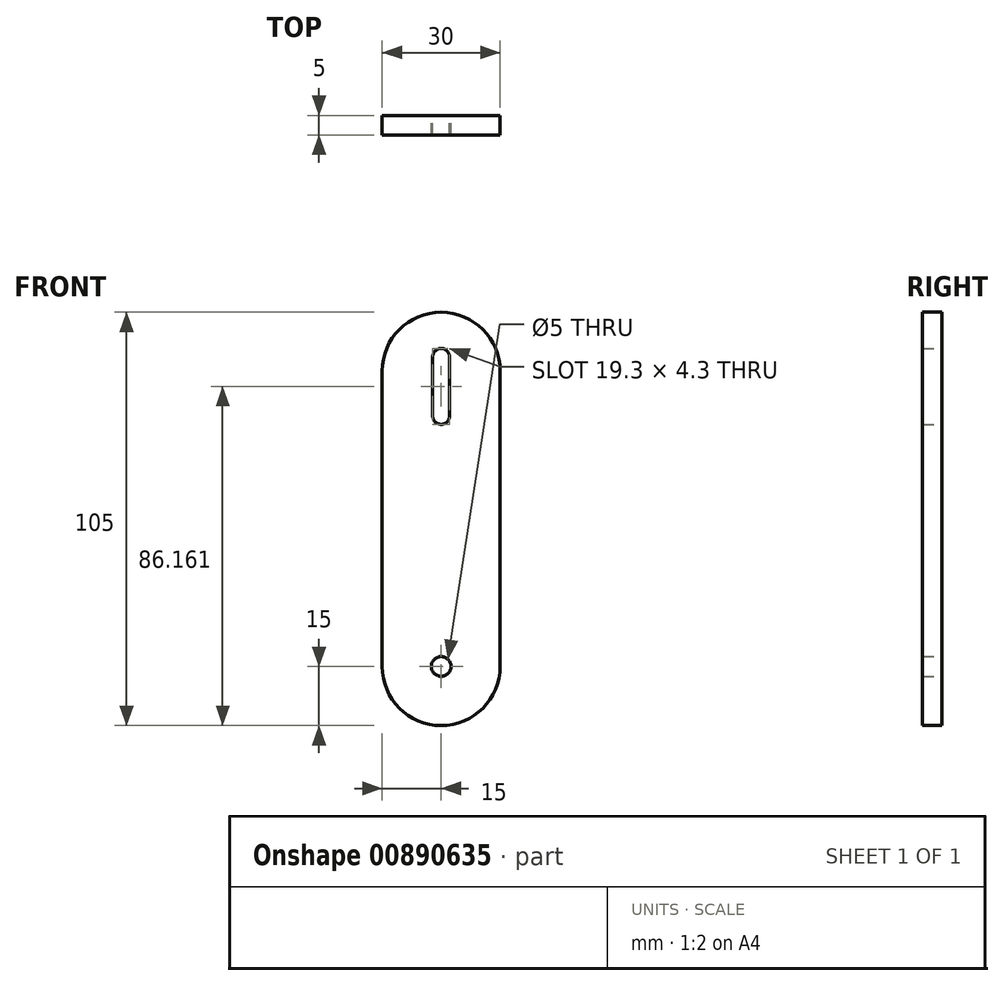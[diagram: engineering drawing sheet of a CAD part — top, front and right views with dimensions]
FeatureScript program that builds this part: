
annotation { "Feature Type Name" : "Feature", "Feature Type Description" : "" }
export const myFeature = defineFeature(function(context is Context, id is Id, definition is map)
    precondition{}
    {
        {
            var Q0;
            Q0=qCreatedBy(makeId("Front.planeOp"),FACE);
            var sketch = newSketch(context, id + "F0", { "sketchPlane" : qUnion([Q0])});
            skLineSegment(sketch, "E0", {"start": v(-15, 0) * mm, "end": v(-15, 75) * mm});
            skLineSegment(sketch, "E1", {"start": v(15, 0) * mm, "end": v(15, 75) * mm});
            skLineSegment(sketch, "E2", {"start": v(-15, 0) * mm, "end": v(0, 0) * mm});
            skLineSegment(sketch, "E3", {"start": v(0, 0) * mm, "end": v(15, 0) * mm});
            skLineSegment(sketch, "E4", {"start": v(-15, 75) * mm, "end": v(15, 75) * mm});
            skArc(sketch, "E5", {"start": v(15, 75) * mm, "mid": v(0, 90) * mm, "end": v(-15, 75) * mm});
            skArc(sketch, "E6", {"start": v(15, 0) * mm, "mid": v(0, -15) * mm, "end": v(-15, 0) * mm});
            skCircle(sketch, "E7", {"center": v(0, 0) * mm, "radius": 2.5 * mm});
            skLineSegment(sketch, "E8", {"start": v(0, 75) * mm, "end": v(2.15, 75) * mm});
            skLineSegment(sketch, "E9", {"start": v(0, 75) * mm, "end": v(-2.15, 75) * mm});
            skLineSegment(sketch, "E10", {"start": v(-2.15, 78.66) * mm, "end": v(-2.15, 63.66) * mm});
            skLineSegment(sketch, "E11", {"start": v(2.15, 78.66) * mm, "end": v(2.15, 63.66) * mm});
            skLineSegment(sketch, "E12", {"start": v(-2.15, 78.66) * mm, "end": v(2.15, 78.66) * mm});
            skLineSegment(sketch, "E13", {"start": v(-2.15, 63.66) * mm, "end": v(2.15, 63.66) * mm});
            skArc(sketch, "E14", {"start": v(-2.15, 78.66) * mm, "mid": v(0, 80.81) * mm, "end": v(2.15, 78.66) * mm});
            skArc(sketch, "E15", {"start": v(2.15, 63.66) * mm, "mid": v(0, 61.51) * mm, "end": v(-2.15, 63.66) * mm});
            skSolve(sketch);
        }
        {
            var Q0;
            Q0 = qSketchRegion(id + "F0", true);
            extrude(context, id + "F1", {"entities" : qUnion([Q0]), "depth" : 5 * mm, "offsetDistance" : 25 * mm});
        }
    });
